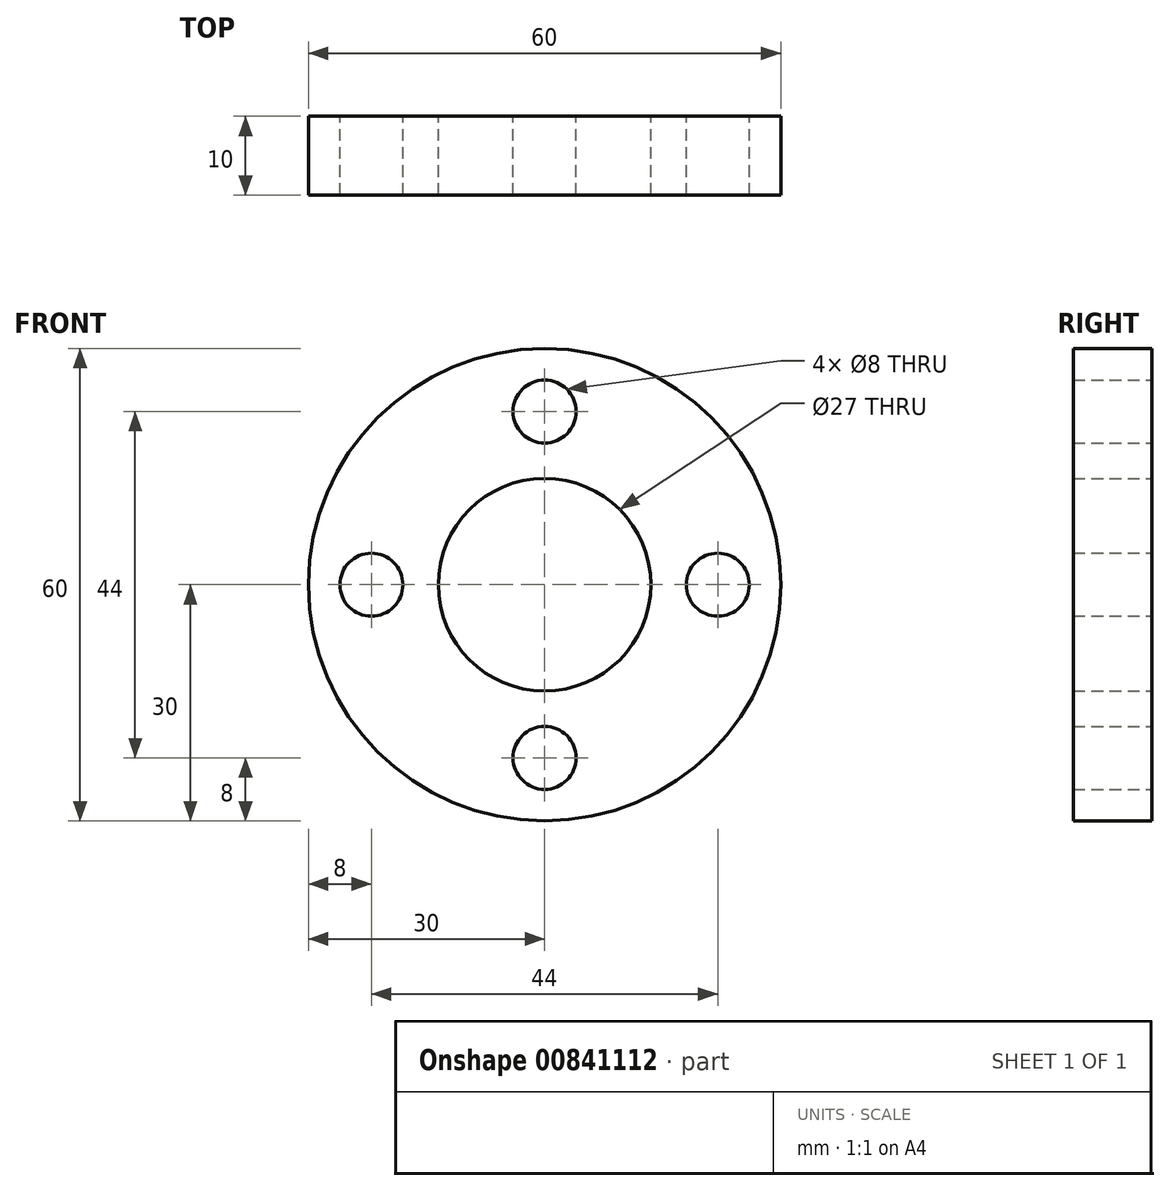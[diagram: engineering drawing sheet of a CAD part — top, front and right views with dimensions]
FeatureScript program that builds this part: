
annotation { "Feature Type Name" : "Feature", "Feature Type Description" : "" }
export const myFeature = defineFeature(function(context is Context, id is Id, definition is map)
    precondition{}
    {
        {
            var Q0;
            Q0=qCreatedBy(makeId("Front.planeOp"),FACE);
            var sketch = newSketch(context, id + "F0", { "sketchPlane" : qUnion([Q0])});
            skCircle(sketch, "E0", {"center": v(0, 0) * mm, "radius": 30 * mm});
            skCircle(sketch, "E1", {"center": v(0, 0) * mm, "radius": 13.5 * mm});
            skCircle(sketch, "E2", {"center": v(0, 22) * mm, "radius": 4 * mm});
            skCircle(sketch, "E3.MirrorC", {"center": v(0, -22) * mm, "radius": 4 * mm});
            skCircle(sketch, "E4", {"center": v(22, 0) * mm, "radius": 4 * mm});
            skCircle(sketch, "E5.MirrorC", {"center": v(-22, 0) * mm, "radius": 4 * mm});
            skSolve(sketch);
        }
        {
            var Q0;
            Q0 = qSketchRegion(id + "F0", true);
            extrude(context, id + "F1", {"entities" : qUnion([Q0]), "depth" : 10 * mm, "offsetDistance" : 25 * mm});
        }
    });
